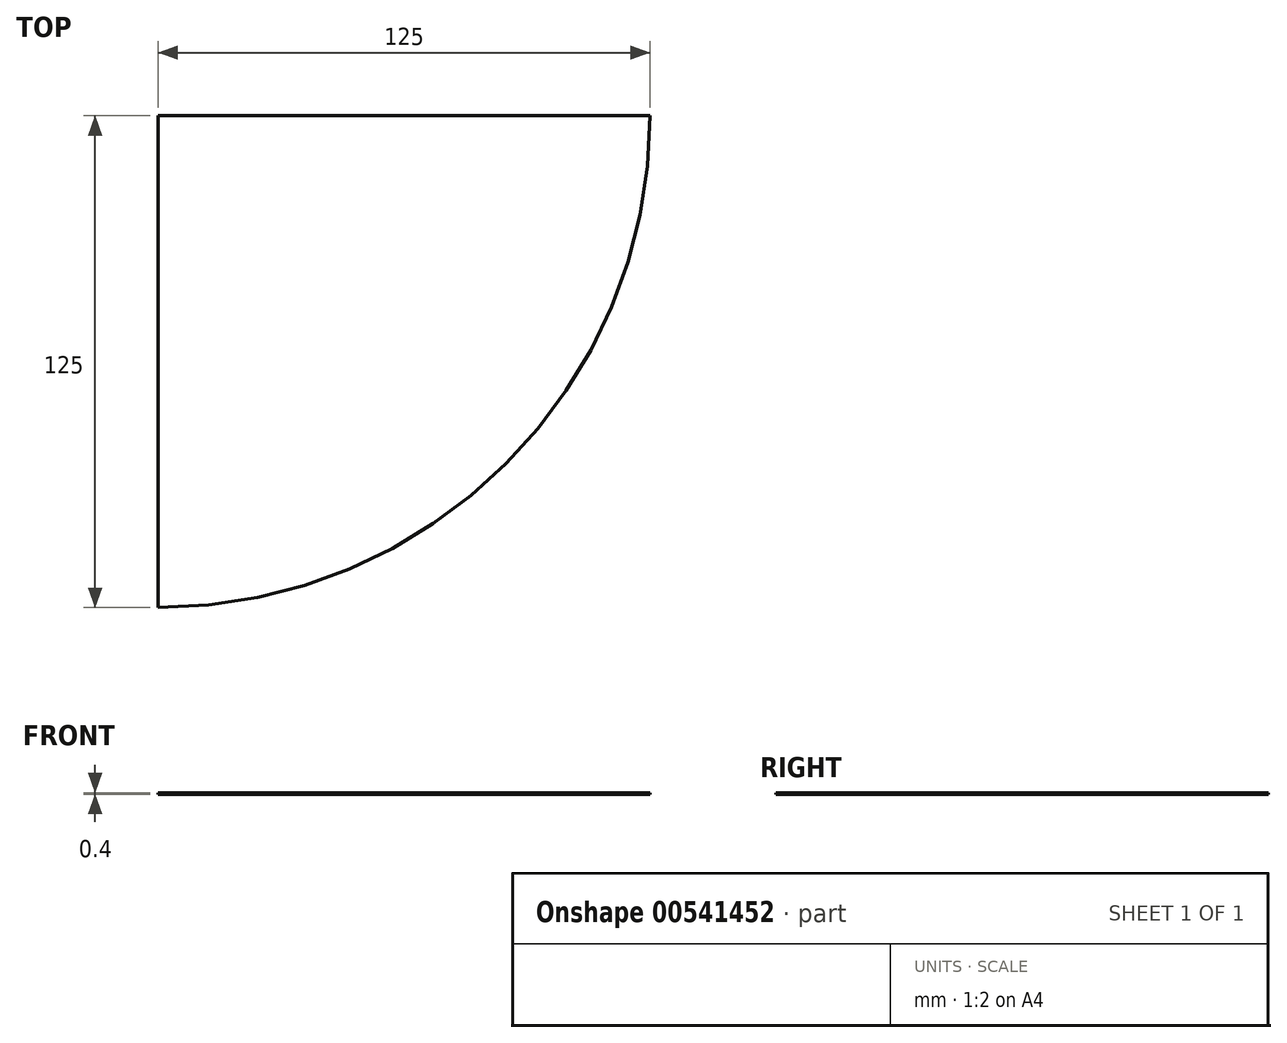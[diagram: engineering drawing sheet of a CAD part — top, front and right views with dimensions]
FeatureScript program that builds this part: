
annotation { "Feature Type Name" : "Feature", "Feature Type Description" : "" }
export const myFeature = defineFeature(function(context is Context, id is Id, definition is map)
    precondition{}
    {
        {
            var Q0;
            Q0=qCreatedBy(makeId("Top.planeOp"),FACE);
            var sketch = newSketch(context, id + "F0", { "sketchPlane" : qUnion([Q0])});
            skPoint(sketch, "E0", {"position": v(125, 0) * mm});
            skPoint(sketch, "E1", {"position": v(0, -125) * mm});
            skArc(sketch, "E2", {"start": v(0, -125) * mm, "mid": v(88.39, -88.39) * mm, "end": v(125, 0) * mm});
            skLineSegment(sketch, "E3", {"start": v(125, 0) * mm, "end": v(0, 0) * mm});
            skLineSegment(sketch, "E4", {"start": v(0, -125) * mm, "end": v(0, 0) * mm});
            skSolve(sketch);
        }
        {
            var Q0;
            Q0=makeQuery(id+"F0.imprint","IMPRINT",FACE,{"disambiguationData":[TD([[makeQuery(id+"F0.imprint","IMPRINT",EDGE,{"derivedFrom":sQuery(id+"F0.wireOp",EDGE,"E2")}),1.0]])]});
            extrude(context, id + "F1", {"entities" : qUnion([Q0]), "depth" : 0.4 * mm, "offsetDistance" : 25 * mm});
        }
    });
